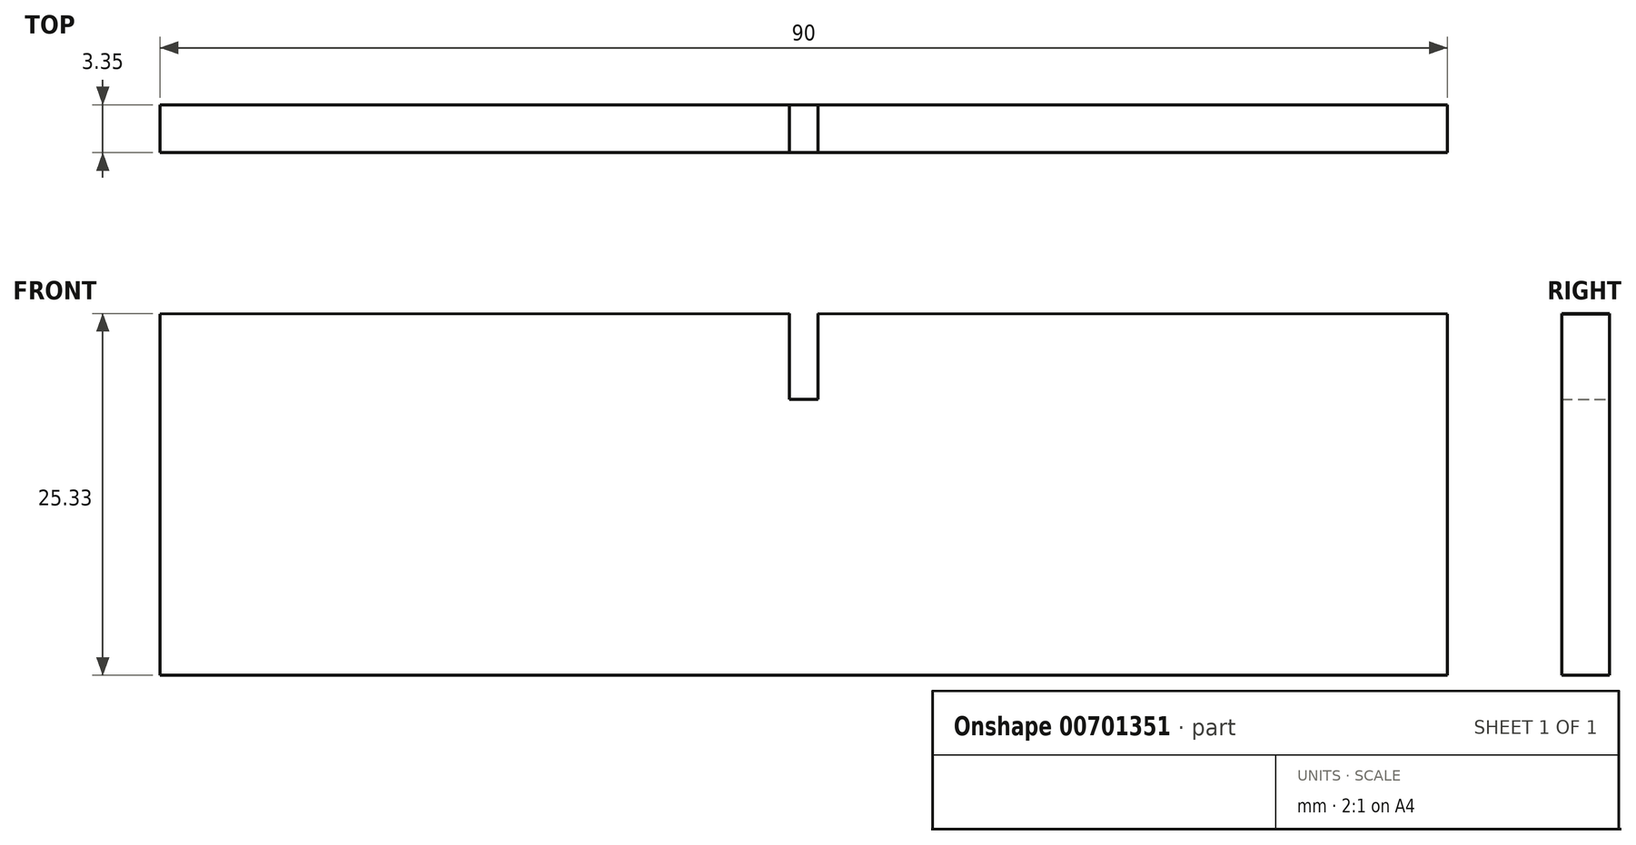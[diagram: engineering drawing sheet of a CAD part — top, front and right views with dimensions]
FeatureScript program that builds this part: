
annotation { "Feature Type Name" : "Feature", "Feature Type Description" : "" }
export const myFeature = defineFeature(function(context is Context, id is Id, definition is map)
    precondition{}
    {
        {
            var Q0;
            Q0=qCreatedBy(makeId("Front.planeOp"),FACE);
            var sketch = newSketch(context, id + "F0", { "sketchPlane" : qUnion([Q0])});
            skLineSegment(sketch, "E0", {"start": v(0, 0) * mm, "end": v(0, 6) * mm});
            skLineSegment(sketch, "E1", {"start": v(0, 0) * mm, "end": v(1, 0) * mm});
            skLineSegment(sketch, "E2", {"start": v(0, 0) * mm, "end": v(-1, 0) * mm});
            skLineSegment(sketch, "E3", {"start": v(-1, 0) * mm, "end": v(-1, 6.03) * mm});
            skLineSegment(sketch, "E4", {"start": v(1, 0) * mm, "end": v(1, 6.03) * mm});
            skLineSegment(sketch, "E5", {"start": v(0, -19.3) * mm, "end": v(-45, -19.3) * mm});
            skLineSegment(sketch, "E6", {"start": v(0, -19.3) * mm, "end": v(45, -19.3) * mm});
            skLineSegment(sketch, "E7", {"start": v(-45, -19.3) * mm, "end": v(-45, 6) * mm});
            skLineSegment(sketch, "E8", {"start": v(45, -19.3) * mm, "end": v(45, 6) * mm});
            skLineSegment(sketch, "E9", {"start": v(-45, 6) * mm, "end": v(-1, 6.03) * mm});
            skLineSegment(sketch, "E10", {"start": v(1, 6.03) * mm, "end": v(45, 6) * mm});
            skSolve(sketch);
        }
        {
            var Q0;
            Q0=makeQuery(id+"F0.imprint","IMPRINT",FACE,{"disambiguationData":[TD([[makeQuery(id+"F0.imprint","IMPRINT",EDGE,{"derivedFrom":sQuery(id+"F0.wireOp",EDGE,"E1")}),-1.0]])]});
            extrude(context, id + "F1", {"entities" : qUnion([Q0]), "depth" : 3.35 * mm, "offsetDistance" : 25 * mm});
        }
    });
